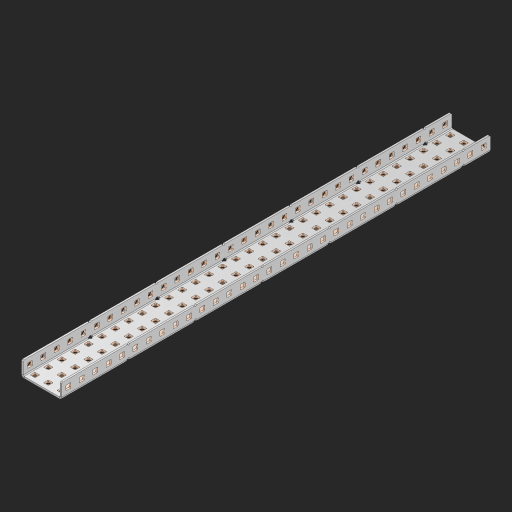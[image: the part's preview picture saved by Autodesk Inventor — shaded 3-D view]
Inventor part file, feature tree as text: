
AUTODESK INVENTOR PART (.ipt)
format: ipt  version: 2023 (Build 270158000, 158)  size: 1,902,080 bytes
history: native  units: in
note: dims shown in document units (in); Inventor stores cm internally (conversion verified against a paired STEP export)
features: other x165, extrude x159, sheet_metal_op x10, sketch x8, mirror x1, pattern_linear x1, chamfer x1
ambient origin geometry x8: Origin, YZ Plane, XZ Plane, XY Plane, X Axis, Y Axis, Z Axis, Center Point
bodies: Solid1 (feature_tree), Body (feature_tree)
feature tree (345):
  other  "Flange Pattern Plane"
  sheet_metal_op  "Flange Pattern"
  sheet_metal_op  "Body Pattern"
  other  "Arc Length"
  mirror  "Notch Mirror"
  pattern_linear  "Notch Pattern"  Spacing1=0.25in  [1 undecoded]
  chamfer  "End Chamfer"
  extrude  "Half Cut"  Depth=0.0625in
  sketch  "Sketch1"  dims[d0=1.5in]
  other  "Plate1"
  sketch  "Sketch2"  dims[d1=16.0in]
  other  "Plate2"
  sheet_metal_op  "Bend1"
  sheet_metal_op  "Corner1"
  sketch  "Sketch3"  dims[d2=0.0625in]
  other  "Flange Pattern Sketch"
  sketch  "Sketch7"  dims[d3=0.0625in]
  other  "Srf1"
  other  "Srf2"
  sketch  "Sketch8"  dims[d4=0.0312in]
  sketch  "Sketch9"  dims[d5=0.125in]
  other  "Srf91"
  sheet_metal_op  "Body Pattern Sketch"
  other  "Srf92"
  sketch  "Sketch13"  dims[d6=0.0625in]
  sketch  "Sketch14"  dims[d7=0.5in d8=90.0deg d9=0.0312in d10=0.25in d11=0.0625in d12=0.0625in d16=0.182in d17=0.02in d18=0.0625in d19=0.0in d20=0.25in d21=0.25in d46=0.172in d47=1.0in d48=0.0in d49=0.182in d50=0.02in d51=0.25in d52=0.25in d53=0.0625in d54=0.0in d55=0.172in d56=1.0in d57=0.0in d60=12.5984in d62=0.5in d63=1.1811in d65=0.5in d85=0.1473in d86=0.1782in d88=0.04in d89=0.0625in d90=0.0in d91=0.04in d92=0.0491in d95=2.5in d96=0.04in d97=0.25in d98=45.0deg d101=0.0in d102=2.497in d131=1.5in d132=12.5984in d134=0.5in d139=0.5in]
  other  "Srf856"
  other  "Srf1310"
  other  "Srf1311"
  other  "Srf1312"
  other  "Srf1376"
  other  "Srf1377"
  other  "Srf1728"
  other  "Srf1755"
  other  "Srf1878"
  other  "Srf1879"
  other  "Srf1880"
  other  "Srf1881"
  other  "Srf1882"
  other  "Srf1883"
  other  "Srf1884"
  other  "Srf1885"
  other  "Srf1886"
  other  "Srf1887"
  other  "Srf1888"
  other  "Srf1889"
  other  "Srf1890"
  other  "Srf1891"
  other  "Srf1892"
  other  "Srf1893"
  other  "Srf1894"
  other  "Srf1895"
  other  "Srf1896"
  other  "Srf1897"
  other  "Srf1898"
  other  "Srf1899"
  other  "Srf1900"
  other  "Srf1901"
  other  "Srf1902"
  other  "Srf1903"
  other  "Srf1904"
  other  "Srf1905"
  other  "Srf1906"
  other  "Srf1907"
  other  "Srf1908"
  other  "Srf1909"
  other  "Srf1910"
  other  "Srf1911"
  other  "Srf1912"
  other  "Srf1913"
  other  "Srf1914"
  other  "Srf1915"
  other  "Srf1916"
  other  "Srf1917"
  other  "Srf1918"
  other  "Srf1919"
  other  "Srf1920"
  other  "Srf1921"
  other  "Srf1922"
  other  "Srf1923"
  other  "Srf1924"
  other  "Srf1925"
  other  "Srf1926"
  other  "Srf1927"
  other  "Srf1928"
  other  "Srf1929"
  other  "Srf1930"
  other  "Srf1931"
  other  "Srf1932"
  other  "Srf1933"
  other  "Srf1934"
  other  "Srf1935"
  other  "Srf1942"
  other  "Srf1943"
  other  "Srf1944"
  other  "Srf1945"
  other  "Srf1946"
  other  "Srf1947"
  other  "Srf1948"
  other  "Srf1949"
  other  "Srf1950"
  other  "Srf1951"
  other  "Srf1952"
  other  "Srf1953"
  other  "Srf1954"
  other  "Srf1955"
  other  "Srf1956"
  other  "Srf1957"
  other  "Srf1958"
  other  "Srf1959"
  other  "Srf1960"
  other  "Srf1961"
  other  "Srf1962"
  other  "Srf1963"
  other  "Srf1964"
  other  "Srf1965"
  other  "Srf1966"
  other  "Srf1967"
  other  "Srf1968"
  other  "Srf1969"
  other  "Srf1970"
  other  "Srf1971"
  other  "Srf1972"
  other  "Srf1973"
  other  "Srf1974"
  other  "Srf1975"
  other  "Srf1976"
  other  "Srf1977"
  other  "Srf1978"
  other  "Srf1979"
  other  "Srf1980"
  other  "Srf1981"
  other  "Srf1982"
  other  "Srf1983"
  other  "Srf1984"
  other  "Srf1985"
  other  "Srf1986"
  other  "Srf1987"
  other  "Srf1988"
  other  "Srf1989"
  other  "Srf1990"
  other  "Srf1991"
  other  "Srf1992"
  other  "Srf1993"
  other  "Srf1994"
  other  "Srf1995"
  other  "Srf1996"
  other  "Srf1997"
  other  "Srf1998"
  other  "Srf1999"
  other  "Srf2000"
  other  "Srf2001"
  other  "Srf2002"
  other  "Srf2003"
  other  "Srf2004"
  other  "Srf2005"
  other  "Srf2006"
  other  "Srf2007"
  other  "Srf2008"
  other  "Srf2009"
  other  "Srf2010"
  other  "Srf2011"
  other  "Srf2012"
  other  "Srf2013"
  other  "Srf2014"
  other  "Srf2015"
  other  "Srf2016"
  other  "Srf2017"
  other  "Srf2018"
  other  "Srf2019"
  other  "Srf2020"
  other  "Srf2021"
  other  "Srf2022"
  other  "Srf2023"
  other  "Srf2024"
  other  "Srf2025"
  other  "Srf2026"
  other  "Srf2027"
  other  "Srf2028"
  other  "Srf2029"
  other  "Srf2030"
  other  "Srf2031"
  sheet_metal_op  "Flange Stamp"
  sheet_metal_op  "Flange Circle"
  sheet_metal_op  "Body Stamp"
  sheet_metal_op  "Body Circle"
  sheet_metal_op  "Notch"
  extrude  "ExtrusionSrf2"  Depth=0.0625in
  extrude  "ExtrusionSrf92"  Depth=1.5in
  extrude  "ExtrusionSrf856"  Depth=0.02in
  extrude  "ExtrusionSrf1310"  Depth=0.0625in
  extrude  "ExtrusionSrf1311"  TaperAngle=0.0deg  [1 undecoded]
  extrude  "ExtrusionSrf1312"  Depth=0.25in
  extrude  "ExtrusionSrf1376"  Depth=0.25in
  extrude  "ExtrusionSrf1377"  Depth=1.5in
  extrude  "ExtrusionSrf1728"  Depth=1.5in TaperAngle=0.0deg
  extrude  "ExtrusionSrf1755"  Depth=1.5in
  extrude  "ExtrusionSrf1878"  Depth=0.02in
  extrude  "ExtrusionSrf1879"  Depth=0.25in
  extrude  "ExtrusionSrf1880"  Depth=0.25in
  extrude  "ExtrusionSrf1881"  Depth=0.0625in
  extrude  "ExtrusionSrf1882"  TaperAngle=0.0deg  [1 undecoded]
  extrude  "ExtrusionSrf1883"  Depth=1.5in
  extrude  "ExtrusionSrf1884"  Depth=1.5in TaperAngle=0.0deg
  extrude  "ExtrusionSrf1885"  Depth=1.5in
  extrude  "ExtrusionSrf1886"  Depth=1.5in
  extrude  "ExtrusionSrf1887"  Depth=1.5in
  extrude  "ExtrusionSrf1888"  Depth=1.5in
  extrude  "ExtrusionSrf1889"  Depth=1.5in
  extrude  "ExtrusionSrf1890"  Depth=0.0625in
  extrude  "ExtrusionSrf1891"  TaperAngle=0.0deg  [1 undecoded]
  extrude  "ExtrusionSrf1892"  Depth=1.5in
  extrude  "ExtrusionSrf1893"  Depth=1.5in
  extrude  "ExtrusionSrf1894"  Depth=1.5in
  extrude  "ExtrusionSrf1895"  Depth=0.25in TaperAngle=45.0deg
  extrude  "ExtrusionSrf1896"  TaperAngle=0.0deg  [1 undecoded]
  extrude  "ExtrusionSrf1897"  Depth=1.5in
  extrude  "ExtrusionSrf1898"  Depth=1.5in
  extrude  "ExtrusionSrf1899"  Depth=1.5in
  extrude  "ExtrusionSrf1900"  Depth=1.5in
  extrude  "ExtrusionSrf1901"  Depth=1.5in
  extrude  "ExtrusionSrf1902"  [1 undecoded]
  extrude  "ExtrusionSrf1903"  [1 undecoded]
  extrude  "ExtrusionSrf1904"  [1 undecoded]
  extrude  "ExtrusionSrf1905"  [1 undecoded]
  extrude  "ExtrusionSrf1906"  [1 undecoded]
  extrude  "ExtrusionSrf1907"  [1 undecoded]
  extrude  "ExtrusionSrf1908"  [1 undecoded]
  extrude  "ExtrusionSrf1909"  [1 undecoded]
  extrude  "ExtrusionSrf1910"  [1 undecoded]
  extrude  "ExtrusionSrf1911"  [1 undecoded]
  extrude  "ExtrusionSrf1912"  [1 undecoded]
  extrude  "ExtrusionSrf1913"  [1 undecoded]
  extrude  "ExtrusionSrf1914"  [1 undecoded]
  extrude  "ExtrusionSrf1915"  [1 undecoded]
  extrude  "ExtrusionSrf1916"  [1 undecoded]
  extrude  "ExtrusionSrf1917"  [1 undecoded]
  extrude  "ExtrusionSrf1918"  [1 undecoded]
  extrude  "ExtrusionSrf1919"  [1 undecoded]
  extrude  "ExtrusionSrf1920"  [1 undecoded]
  extrude  "ExtrusionSrf1921"  [1 undecoded]
  extrude  "ExtrusionSrf1922"  [1 undecoded]
  extrude  "ExtrusionSrf1923"  [1 undecoded]
  extrude  "ExtrusionSrf1924"  [1 undecoded]
  extrude  "ExtrusionSrf1925"  [1 undecoded]
  extrude  "ExtrusionSrf1926"  [1 undecoded]
  extrude  "ExtrusionSrf1927"  [1 undecoded]
  extrude  "ExtrusionSrf1928"  [1 undecoded]
  extrude  "ExtrusionSrf1929"  [1 undecoded]
  extrude  "ExtrusionSrf1930"  [1 undecoded]
  extrude  "ExtrusionSrf1931"  [1 undecoded]
  extrude  "ExtrusionSrf1932"  [1 undecoded]
  extrude  "ExtrusionSrf1933"  [1 undecoded]
  extrude  "ExtrusionSrf1934"  [1 undecoded]
  extrude  "ExtrusionSrf1935"  [1 undecoded]
  extrude  "ExtrusionSrf1942"  [1 undecoded]
  extrude  "ExtrusionSrf1943"  [1 undecoded]
  extrude  "ExtrusionSrf1944"  [1 undecoded]
  extrude  "ExtrusionSrf1945"  [1 undecoded]
  extrude  "ExtrusionSrf1946"  [1 undecoded]
  extrude  "ExtrusionSrf1947"  [1 undecoded]
  extrude  "ExtrusionSrf1948"  [1 undecoded]
  extrude  "ExtrusionSrf1949"  [1 undecoded]
  extrude  "ExtrusionSrf1950"  [1 undecoded]
  extrude  "ExtrusionSrf1951"  [1 undecoded]
  extrude  "ExtrusionSrf1952"  [1 undecoded]
  extrude  "ExtrusionSrf1953"  [1 undecoded]
  extrude  "ExtrusionSrf1954"  [1 undecoded]
  extrude  "ExtrusionSrf1955"  [1 undecoded]
  extrude  "ExtrusionSrf1956"  [1 undecoded]
  extrude  "ExtrusionSrf1957"  [1 undecoded]
  extrude  "ExtrusionSrf1958"  [1 undecoded]
  extrude  "ExtrusionSrf1959"  [1 undecoded]
  extrude  "ExtrusionSrf1960"  [1 undecoded]
  extrude  "ExtrusionSrf1961"  [1 undecoded]
  extrude  "ExtrusionSrf1962"  [1 undecoded]
  extrude  "ExtrusionSrf1963"  [1 undecoded]
  extrude  "ExtrusionSrf1964"  [1 undecoded]
  extrude  "ExtrusionSrf1965"  [1 undecoded]
  extrude  "ExtrusionSrf1966"  [1 undecoded]
  extrude  "ExtrusionSrf1967"  [1 undecoded]
  extrude  "ExtrusionSrf1968"  [1 undecoded]
  extrude  "ExtrusionSrf1969"  [1 undecoded]
  extrude  "ExtrusionSrf1970"  [1 undecoded]
  extrude  "ExtrusionSrf1971"  [1 undecoded]
  extrude  "ExtrusionSrf1972"  [1 undecoded]
  extrude  "ExtrusionSrf1973"  [1 undecoded]
  extrude  "ExtrusionSrf1974"  [1 undecoded]
  extrude  "ExtrusionSrf1975"  [1 undecoded]
  extrude  "ExtrusionSrf1976"  [1 undecoded]
  extrude  "ExtrusionSrf1977"  [1 undecoded]
  extrude  "ExtrusionSrf1978"  [1 undecoded]
  extrude  "ExtrusionSrf1979"  [1 undecoded]
  extrude  "ExtrusionSrf1980"  [1 undecoded]
  extrude  "ExtrusionSrf1981"  [1 undecoded]
  extrude  "ExtrusionSrf1982"  [1 undecoded]
  extrude  "ExtrusionSrf1983"  [1 undecoded]
  extrude  "ExtrusionSrf1984"  [1 undecoded]
  extrude  "ExtrusionSrf1985"  [1 undecoded]
  extrude  "ExtrusionSrf1986"  [1 undecoded]
  extrude  "ExtrusionSrf1987"  [1 undecoded]
  extrude  "ExtrusionSrf1988"  [1 undecoded]
  extrude  "ExtrusionSrf1989"  [1 undecoded]
  extrude  "ExtrusionSrf1990"  [1 undecoded]
  extrude  "ExtrusionSrf1991"  [1 undecoded]
  extrude  "ExtrusionSrf1992"  [1 undecoded]
  extrude  "ExtrusionSrf1993"  [1 undecoded]
  extrude  "ExtrusionSrf1994"  [1 undecoded]
  extrude  "ExtrusionSrf1995"  [1 undecoded]
  extrude  "ExtrusionSrf1996"  [1 undecoded]
  extrude  "ExtrusionSrf1997"  [1 undecoded]
  extrude  "ExtrusionSrf1998"  [1 undecoded]
  extrude  "ExtrusionSrf1999"  [1 undecoded]
  extrude  "ExtrusionSrf2000"  [1 undecoded]
  extrude  "ExtrusionSrf2001"  [1 undecoded]
  extrude  "ExtrusionSrf2002"  [1 undecoded]
  extrude  "ExtrusionSrf2003"  [1 undecoded]
  extrude  "ExtrusionSrf2004"  [1 undecoded]
  extrude  "ExtrusionSrf2005"  [1 undecoded]
  extrude  "ExtrusionSrf2006"  [1 undecoded]
  extrude  "ExtrusionSrf2007"  [1 undecoded]
  extrude  "ExtrusionSrf2008"  [1 undecoded]
  extrude  "ExtrusionSrf2009"  [1 undecoded]
  extrude  "ExtrusionSrf2010"  [1 undecoded]
  extrude  "ExtrusionSrf2011"  [1 undecoded]
  extrude  "ExtrusionSrf2012"  [1 undecoded]
  extrude  "ExtrusionSrf2013"  [1 undecoded]
  extrude  "ExtrusionSrf2014"  [1 undecoded]
  extrude  "ExtrusionSrf2015"  [1 undecoded]
  extrude  "ExtrusionSrf2016"  [1 undecoded]
  extrude  "ExtrusionSrf2017"  [1 undecoded]
  extrude  "ExtrusionSrf2018"  [1 undecoded]
  extrude  "ExtrusionSrf2019"  [1 undecoded]
  extrude  "ExtrusionSrf2020"  [1 undecoded]
  extrude  "ExtrusionSrf2021"  [1 undecoded]
  extrude  "ExtrusionSrf2022"  [1 undecoded]
  extrude  "ExtrusionSrf2023"  [1 undecoded]
  extrude  "ExtrusionSrf2024"  [1 undecoded]
  extrude  "ExtrusionSrf2025"  [1 undecoded]
  extrude  "ExtrusionSrf2026"  [1 undecoded]
  extrude  "ExtrusionSrf2027"  [1 undecoded]
  extrude  "ExtrusionSrf2028"  [1 undecoded]
  extrude  "ExtrusionSrf2029"  [1 undecoded]
  extrude  "ExtrusionSrf2030"  [1 undecoded]
  extrude  "ExtrusionSrf2031"  [1 undecoded]
note: 129 required parameter values undecoded (feature->parameter linkage not recoverable at this tier; creation-order binding heuristic only, values carry confidence <= 0.55)
